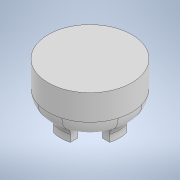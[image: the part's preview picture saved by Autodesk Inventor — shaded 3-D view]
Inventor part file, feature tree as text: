
AUTODESK INVENTOR PART (.ipt)
format: ipt  version: 2022 (Build 260153000, 153)  size: 188,416 bytes
history: native  units: in
note: dims shown in document units (in); Inventor stores cm internally (conversion verified against a paired STEP export)
features: extrude x3, sketch x3, fillet x2
ambient origin geometry x8: Origin, YZ Plane, XZ Plane, XY Plane, X Axis, Y Axis, Z Axis, Center Point
bodies: Solid1 (feature_tree)
feature tree (8):
  extrude  "Extrusion1"  Depth=0.3937in TaperAngle=0.0deg
  sketch  "Sketch2"  dims[d3=0.2756in d4=0.0787in]
  extrude  "Extrusion3"  Depth=0.0787in
  extrude  "Extrusion4"  Depth=0.0394in
  fillet  "Fillet1"  Radius=0.0787in
  fillet  "Fillet2"  Radius=0.0787in
  sketch  "Sketch1"  dims[d0=0.3937in d1=0.1969in d2=0.0in]
  sketch  "Sketch3"  dims[d5=0.0787in d6=0.0787in d7=0.0787in d8=0.0787in d9=0.0787in d10=0.0787in d11=0.0787in d14=0.0394in d15=0.0in d16=0.1181in d17=0.0in d18=0.0787in d19=0.0394in]
